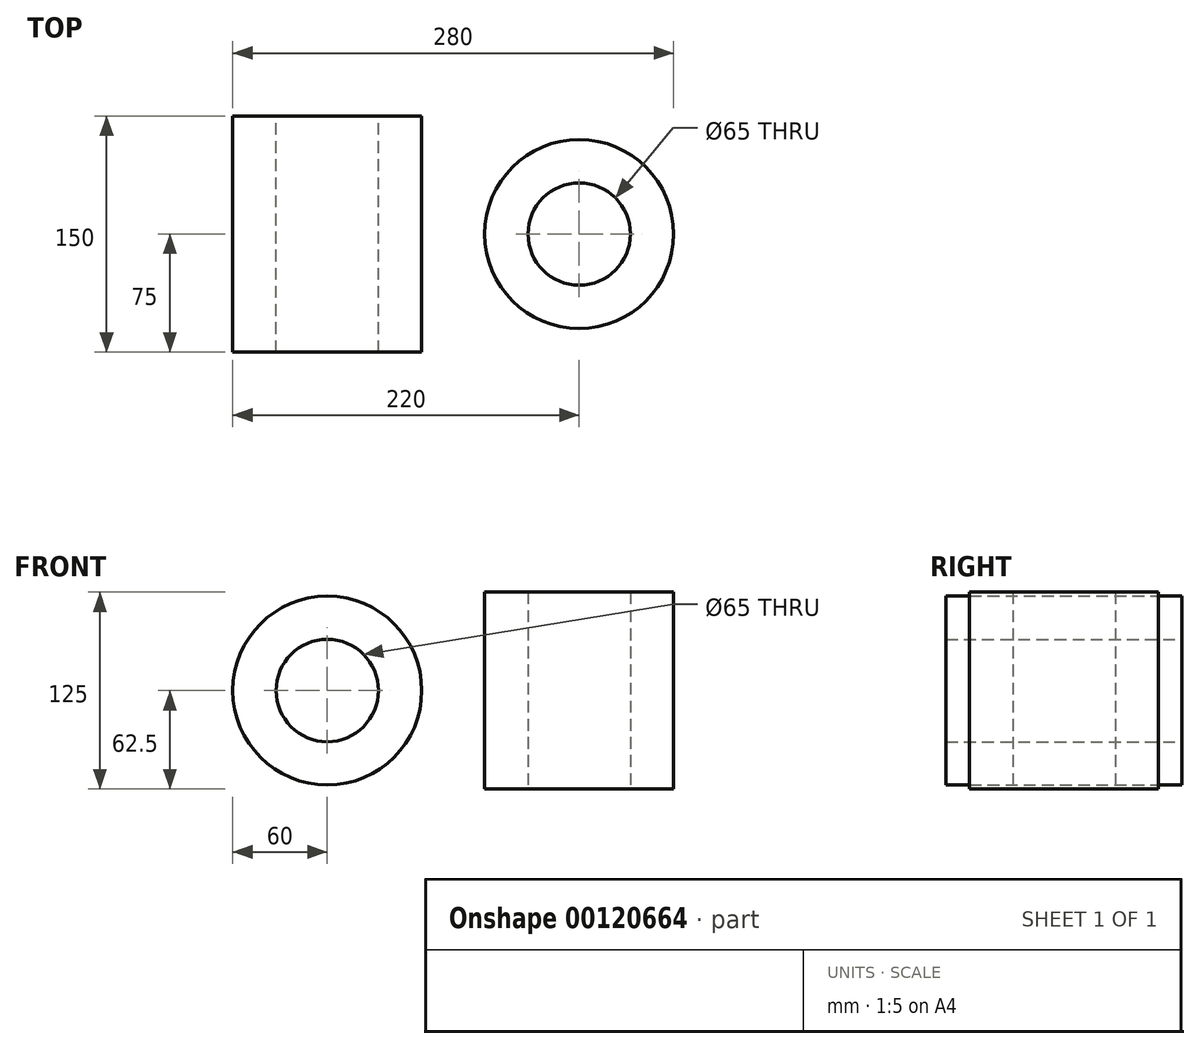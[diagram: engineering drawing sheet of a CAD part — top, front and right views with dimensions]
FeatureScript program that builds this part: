
annotation { "Feature Type Name" : "Feature", "Feature Type Description" : "" }
export const myFeature = defineFeature(function(context is Context, id is Id, definition is map)
    precondition{}
    {
        {
            var Q0;
            Q0=qCreatedBy(makeId("Top.planeOp"),FACE);
            var sketch = newSketch(context, id + "F0", { "sketchPlane" : qUnion([Q0])});
            skCircle(sketch, "E0", {"center": v(0, 0) * mm, "radius": 60 * mm});
            skCircle(sketch, "E1", {"center": v(0, 0) * mm, "radius": 32.5 * mm});
            skSolve(sketch);
        }
        {
            var Q0;
            Q0=makeQuery(id+"F0.imprint","IMPRINT",FACE,{"disambiguationData":[TD([[makeQuery(id+"F0.imprint","IMPRINT",EDGE,{"derivedFrom":sQuery(id+"F0.wireOp",EDGE,"E0")}),1.0]])]});
            extrude(context, id + "F1", {"entities" : qUnion([Q0]), "endBound" : BoundingType.SYMMETRIC, "depth" : 125 * mm});
        }
        {
            var Q0;
            Q0=qCreatedBy(makeId("Front.planeOp"),FACE);
            var sketch = newSketch(context, id + "F2", { "sketchPlane" : qUnion([Q0])});
            skCircle(sketch, "E2", {"center": v(-160, 0) * mm, "radius": 60 * mm});
            skCircle(sketch, "E3", {"center": v(-160, 0) * mm, "radius": 32.5 * mm});
            skSolve(sketch);
        }
        {
            var Q0;
            Q0=makeQuery(id+"F2.imprint","IMPRINT",FACE,{"disambiguationData":[TD([[makeQuery(id+"F2.imprint","IMPRINT",EDGE,{"derivedFrom":sQuery(id+"F2.wireOp",EDGE,"E2")}),1.0]])]});
            extrude(context, id + "F3", {"entities" : qUnion([Q0]), "endBound" : BoundingType.SYMMETRIC, "depth" : 150 * mm});
        }
    });
